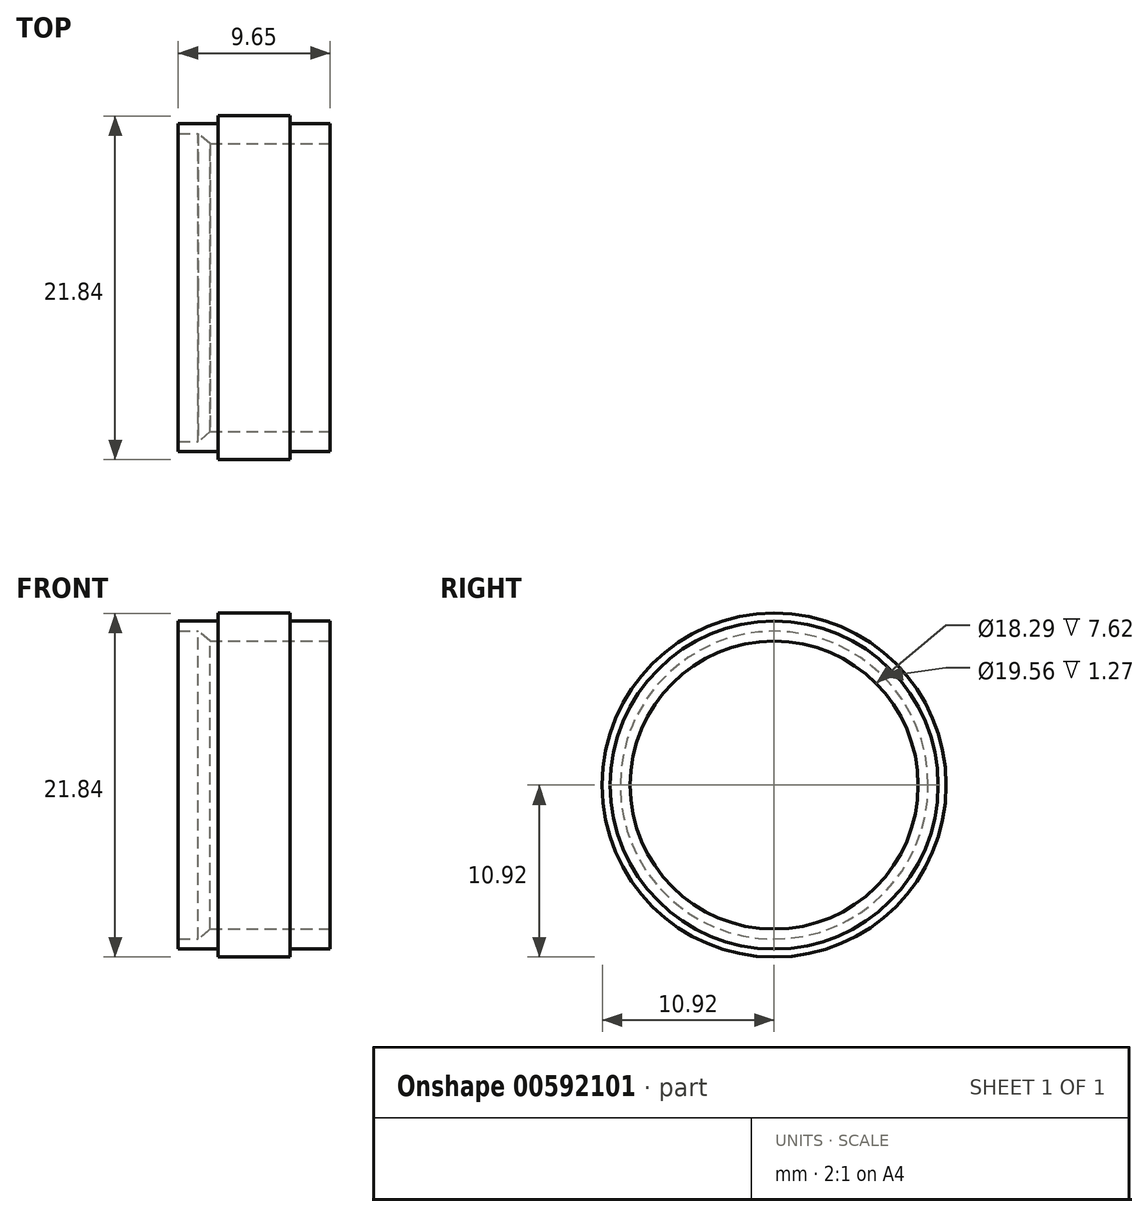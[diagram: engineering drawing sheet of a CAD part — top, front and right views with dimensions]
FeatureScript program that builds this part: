
annotation { "Feature Type Name" : "Feature", "Feature Type Description" : "" }
export const myFeature = defineFeature(function(context is Context, id is Id, definition is map)
    precondition{}
    {
        {
            var Q0;
            Q0=qCreatedBy(makeId("Front.planeOp"),FACE);
            var sketch = newSketch(context, id + "F0", { "sketchPlane" : qUnion([Q0])});
            skLineSegment(sketch, "E0", {"start": v(0, 9.14) * mm, "end": v(-7.62, 9.14) * mm});
            skLineSegment(sketch, "E1", {"start": v(0, 9.14) * mm, "end": v(0, 10.41) * mm});
            skLineSegment(sketch, "E2", {"start": v(0, 10.41) * mm, "end": v(-2.54, 10.41) * mm});
            skLineSegment(sketch, "E3", {"start": v(-2.54, 10.41) * mm, "end": v(-2.54, 10.92) * mm});
            skLineSegment(sketch, "E4", {"start": v(-2.54, 10.92) * mm, "end": v(-7.11, 10.92) * mm});
            skLineSegment(sketch, "E5", {"start": v(-7.11, 10.92) * mm, "end": v(-7.11, 10.41) * mm});
            skLineSegment(sketch, "E6", {"start": v(-7.11, 10.41) * mm, "end": v(-9.65, 10.41) * mm});
            skLineSegment(sketch, "E7", {"start": v(-9.65, 10.41) * mm, "end": v(-9.65, 9.78) * mm});
            skLineSegment(sketch, "E8", {"start": v(-9.65, 9.78) * mm, "end": v(-8.38, 9.78) * mm});
            skLineSegment(sketch, "E9", {"start": v(-8.38, 9.78) * mm, "end": v(-7.62, 9.14) * mm});
            skLineSegment(sketch, "E10", {"start": v(0, 0) * mm, "end": v(-6.08, 0) * mm});
            skSolve(sketch);
        }
        {
            var Q0;
            Q0=makeQuery(id+"F0.imprint","IMPRINT",FACE,{"disambiguationData":[TD([[makeQuery(id+"F0.imprint","IMPRINT",EDGE,{"derivedFrom":sQuery(id+"F0.wireOp",EDGE,"E0")}),-1.0]])]});
            var Q1;
            Q1=sQuery(id+"F0.wireOp",EDGE,"E10");
            revolve(context, id + "F1", {"entities" : qUnion([Q0]), "axis" : qUnion([Q1]), "revolveType" : RevolveType.FULL});
        }
    });
